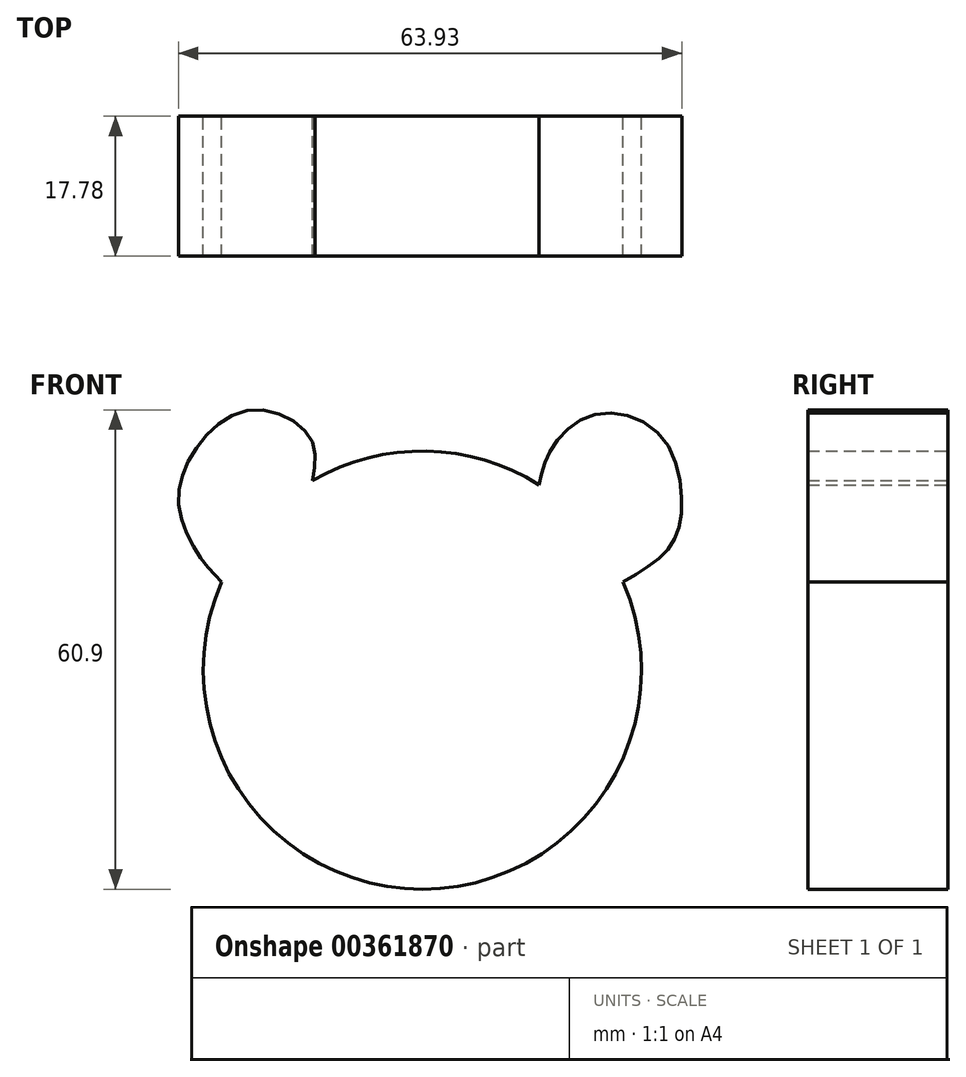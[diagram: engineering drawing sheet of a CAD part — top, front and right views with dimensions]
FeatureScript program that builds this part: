
annotation { "Feature Type Name" : "Feature", "Feature Type Description" : "" }
export const myFeature = defineFeature(function(context is Context, id is Id, definition is map)
    precondition{}
    {
        {
            var Q0;
            Q0=qCreatedBy(makeId("Front.planeOp"),FACE);
            var sketch = newSketch(context, id + "F0", { "sketchPlane" : qUnion([Q0])});
            skCircle(sketch, "E0", {"center": v(0, 0) * mm, "radius": 27.83 * mm});
            skFitSpline(sketch, "E1", {"points": [v(-13.94, 24.09) * mm, v(-14.34, 29.67) * mm, v(-21.65, 33.04) * mm, v(-28.69, 28.26) * mm, v(-30.94, 20.95) * mm, v(-28.12, 14.2) * mm, v(-25.49, 11.18) * mm], "startDerivative": vector(6.38, 38.67) * mm, "endDerivative": vector(20.24, -20.2) * mm});
            skFitSpline(sketch, "E2", {"points": [v(14.84, 23.54) * mm, v(16.31, 27.98) * mm, v(21.94, 32.48) * mm, v(30.37, 29.67) * mm, v(32.9, 20.1) * mm, v(30.94, 15.05) * mm, v(25.49, 11.18) * mm], "startDerivative": vector(6.61, 32.2) * mm, "endDerivative": vector(-38.01, -22.05) * mm});
            skSolve(sketch);
        }
        {
            var Q0;
            Q0=qCreatedBy(makeId("Front.planeOp"),FACE);
            var sketch = newSketch(context, id + "F1", { "sketchPlane" : qUnion([Q0])});
            skFitSpline(sketch, "E3", {"points": [v(-4.5, -3.23) * mm, v(0, -4.92) * mm, v(4.78, -2.95) * mm, v(5.9, -7.73) * mm, v(0, -10.63) * mm, v(-5.44, -8.87) * mm, v(-4.5, -3.23) * mm]});
            skFitSpline(sketch, "E4", {"points": [v(0, -10.63) * mm, v(0, -15.6) * mm, v(-3.1, -18.23) * mm, v(-8.66, -16.76) * mm, v(-9.24, -10.63) * mm], "startDerivative": vector(3.11, -21.79) * mm, "endDerivative": vector(3.35, 26) * mm});
            skFitSpline(sketch, "E5", {"points": [v(0, -15.6) * mm, v(3.33, -18.23) * mm, v(7.7, -16.76) * mm, v(9.46, -10.63) * mm], "startDerivative": vector(9.6, -11.33) * mm, "endDerivative": vector(1.86, 18.78) * mm});
            skFitSpline(sketch, "E6", {"points": [v(-18.6, 15.97) * mm, v(-9.55, 18.6) * mm, v(-5.44, 14.8) * mm, v(-12.47, 10.43) * mm, v(-18.01, 10.43) * mm, v(-20.63, 12.76) * mm, v(-18.6, 15.97) * mm]});
            skFitSpline(sketch, "E7", {"points": [v(6.6, 14.8) * mm, v(9.46, 18.6) * mm, v(17.62, 18.6) * mm, v(18.4, 14.8) * mm, v(16.57, 11) * mm, v(9.46, 10.47) * mm, v(6.6, 14.8) * mm]});
            skSolve(sketch);
        }
        {
            var Q0;
            Q0 = qSketchRegion(id + "F0", true);
            extrude(context, id + "F2", {"entities" : qUnion([Q0]), "depth" : 17.78 * mm});
        }
        {
            var Q0;
            Q0=sQuery(id+"F1.wireOp",EDGE,"E6");
            var Q1;
            Q1=sQuery(id+"F1.wireOp",EDGE,"E7");
            extrude(context, id + "F3", {"bodyType" : ToolBodyType.SURFACE, "surfaceEntities" : qUnion([Q0, Q1]), "depth" : 25.9 * mm});
        }
    });
